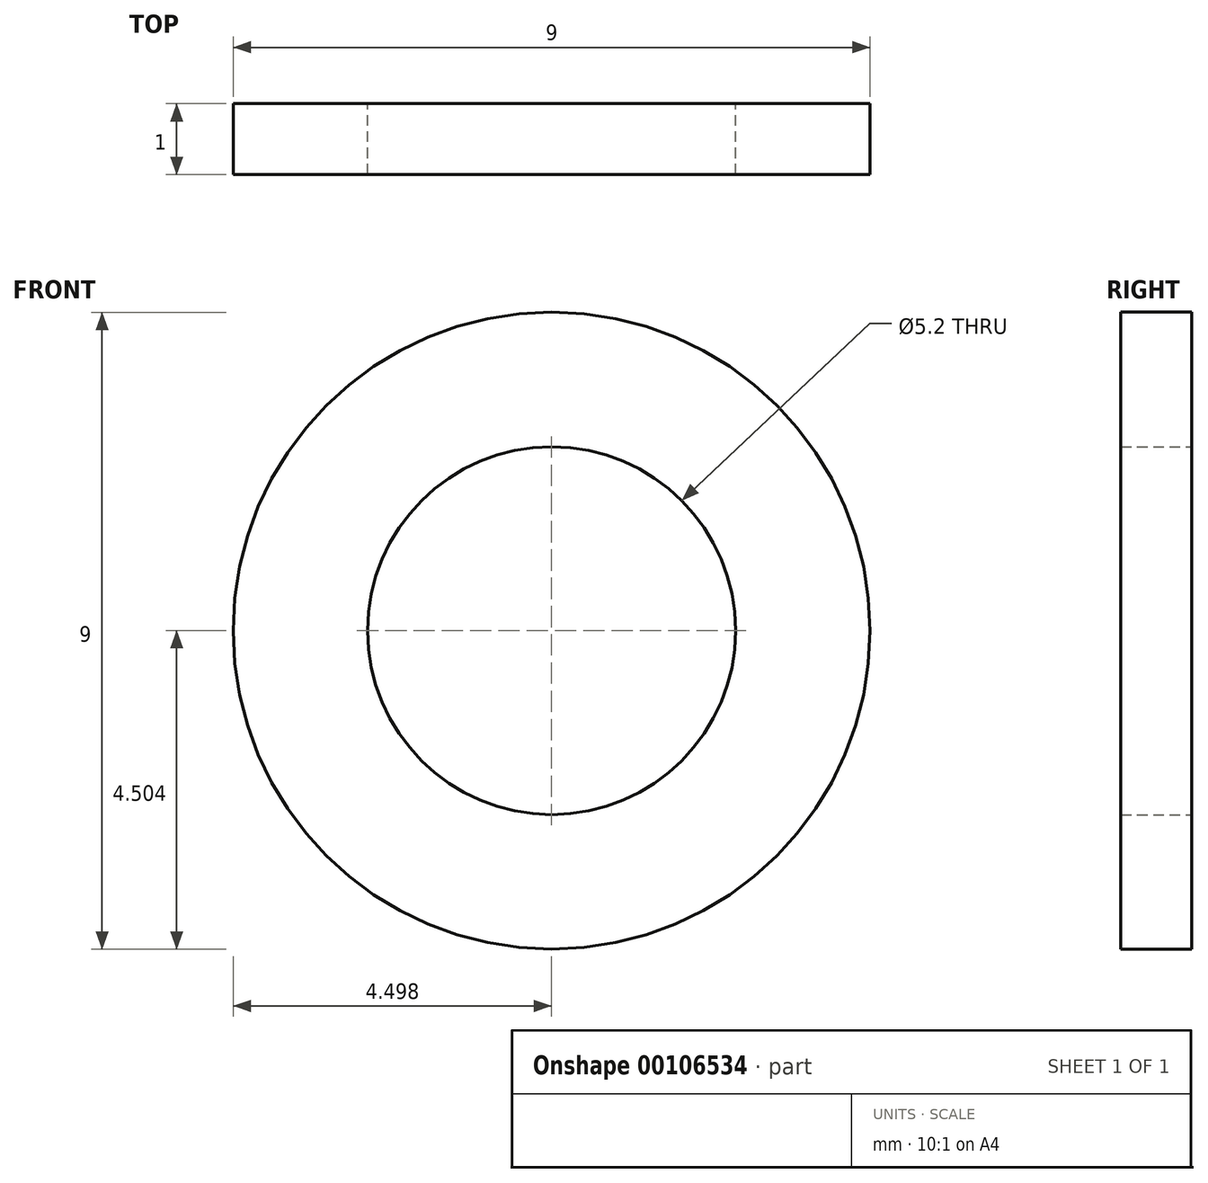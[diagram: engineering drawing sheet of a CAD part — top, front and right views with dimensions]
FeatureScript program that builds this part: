
annotation { "Feature Type Name" : "Feature", "Feature Type Description" : "" }
export const myFeature = defineFeature(function(context is Context, id is Id, definition is map)
    precondition{}
    {
        {
            var Q0;
            Q0=qCreatedBy(makeId("Front.planeOp"),FACE);
            var sketch = newSketch(context, id + "F0", { "sketchPlane" : qUnion([Q0])});
            skCircle(sketch, "E0", {"center": v(-45.46, 32.57) * mm, "radius": 4.5 * mm});
            skCircle(sketch, "E1", {"center": v(-45.46, 32.57) * mm, "radius": 2.6 * mm});
            skSolve(sketch);
        }
        {
            var Q0;
            Q0=makeQuery(id+"F0.imprint","IMPRINT",FACE,{"disambiguationData":[TD([[makeQuery(id+"F0.imprint","IMPRINT",EDGE,{"derivedFrom":sQuery(id+"F0.wireOp",EDGE,"E0")}),1.0]])]});
            var Q1;
            Q1=sQuery(id+"F0.wireOp",EDGE,"E0");
            extrude(context, id + "F1", {"entities" : qUnion([Q0]), "surfaceEntities" : qUnion([Q1]), "depth" : 1 * mm});
        }
    });
